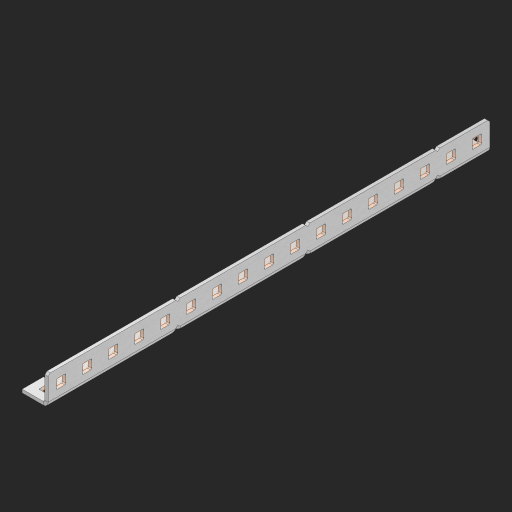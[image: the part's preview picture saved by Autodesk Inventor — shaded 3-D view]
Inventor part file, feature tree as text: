
AUTODESK INVENTOR PART (.ipt)
format: ipt  version: 2023 (Build 270158000, 158)  size: 903,168 bytes
history: native  units: in
note: dims shown in document units (in); Inventor stores cm internally (conversion verified against a paired STEP export)
features: other x199, extrude x49, sheet_metal_op x11, sketch x10, pattern_linear x2, mirror x1, chamfer x1
ambient origin geometry x8: Origin, YZ Plane, XZ Plane, XY Plane, X Axis, Y Axis, Z Axis, Center Point
bodies: Solid1 (feature_tree), Body (feature_tree)
feature tree (273):
  other  "Alu Half C 1x2x1x17"
  other  "Table"
  other  "Alu C 1x2x1x35"
  other  "Alu C 1x2x1x34"
  other  "Alu C 1x2x1x33"
  other  "Alu C 1x2x1x32"
  other  "Alu C 1x2x1x31"
  other  "Alu C 1x2x1x30"
  other  "Alu C 1x2x1x29"
  other  "Alu C 1x2x1x28"
  other  "Alu C 1x2x1x27"
  other  "Alu C 1x2x1x26"
  other  "Alu C 1x2x1x25"
  other  "Alu C 1x2x1x24"
  other  "Alu C 1x2x1x23"
  other  "Alu C 1x2x1x22"
  other  "Alu C 1x2x1x21"
  other  "Alu C 1x2x1x20"
  other  "Alu C 1x2x1x19"
  other  "Alu C 1x2x1x18"
  other  "Alu C 1x2x1x17"
  other  "Alu C 1x2x1x16"
  other  "Alu C 1x2x1x15"
  other  "Alu C 1x2x1x14"
  other  "Alu C 1x2x1x13"
  other  "Alu C 1x2x1x12"
  other  "Alu C 1x2x1x11"
  other  "Alu C 1x2x1x10"
  other  "Alu C 1x2x1x9"
  other  "Alu C 1x2x1x8"
  other  "Alu C 1x2x1x7"
  other  "Alu C 1x2x1x6"
  other  "Alu C 1x2x1x5"
  other  "Alu C 1x2x1x4"
  other  "Alu C 1x2x1x3"
  other  "Alu C 1x2x1x2"
  other  "Alu C 1x2x1x1"
  other  "Steel C 1x2x1x35"
  other  "Steel C 1x2x1x34"
  other  "Steel C 1x2x1x33"
  other  "Steel C 1x2x1x32"
  other  "Steel C 1x2x1x31"
  other  "Steel C 1x2x1x30"
  other  "Steel C 1x2x1x29"
  other  "Steel C 1x2x1x28"
  other  "Steel C 1x2x1x27"
  other  "Steel C 1x2x1x26"
  other  "Steel C 1x2x1x25"
  other  "Steel C 1x2x1x24"
  other  "Steel C 1x2x1x23"
  other  "Steel C 1x2x1x22"
  other  "Steel C 1x2x1x21"
  other  "Steel C 1x2x1x20"
  other  "Steel C 1x2x1x19"
  other  "Steel C 1x2x1x18"
  other  "Steel C 1x2x1x17"
  other  "Steel C 1x2x1x16"
  other  "Steel C 1x2x1x15"
  other  "Steel C 1x2x1x14"
  other  "Steel C 1x2x1x13"
  other  "Steel C 1x2x1x12"
  other  "Steel C 1x2x1x11"
  other  "Steel C 1x2x1x10"
  other  "Steel C 1x2x1x9"
  other  "Steel C 1x2x1x8"
  other  "Steel C 1x2x1x7"
  other  "Steel C 1x2x1x6"
  other  "Steel C 1x2x1x5"
  other  "Steel C 1x2x1x4"
  other  "Steel C 1x2x1x3"
  other  "Steel C 1x2x1x2"
  other  "Steel C 1x2x1x1"
  other  "Alu Half C 1x2x1x35"
  other  "Alu Half C 1x2x1x34"
  other  "Alu Half C 1x2x1x33"
  other  "Alu Half C 1x2x1x32"
  other  "Alu Half C 1x2x1x31"
  other  "Alu Half C 1x2x1x30"
  other  "Alu Half C 1x2x1x29"
  other  "Alu Half C 1x2x1x28"
  other  "Alu Half C 1x2x1x27"
  other  "Alu Half C 1x2x1x26"
  other  "Alu Half C 1x2x1x25"
  other  "Alu Half C 1x2x1x24"
  other  "Alu Half C 1x2x1x23"
  other  "Alu Half C 1x2x1x22"
  other  "Alu Half C 1x2x1x21"
  other  "Alu Half C 1x2x1x20"
  other  "Alu Half C 1x2x1x19"
  other  "Alu Half C 1x2x1x18"
  other  "Alu Half C 1x2x1x16"
  other  "Alu Half C 1x2x1x15"
  other  "Alu Half C 1x2x1x14"
  other  "Alu Half C 1x2x1x13"
  other  "Alu Half C 1x2x1x12"
  other  "Alu Half C 1x2x1x11"
  other  "Alu Half C 1x2x1x10"
  other  "Alu Half C 1x2x1x9"
  other  "Alu Half C 1x2x1x8"
  other  "Alu Half C 1x2x1x7"
  other  "Alu Half C 1x2x1x6"
  other  "Alu Half C 1x2x1x5"
  other  "Alu Half C 1x2x1x4"
  other  "Alu Half C 1x2x1x3"
  other  "Alu Half C 1x2x1x2"
  other  "Alu Half C 1x2x1x1"
  other  "Steel Half C 1x2x1x35"
  other  "Steel Half C 1x2x1x34"
  other  "Steel Half C 1x2x1x33"
  other  "Steel Half C 1x2x1x32"
  other  "Steel Half C 1x2x1x31"
  other  "Steel Half C 1x2x1x30"
  other  "Steel Half C 1x2x1x29"
  other  "Steel Half C 1x2x1x28"
  other  "Steel Half C 1x2x1x27"
  other  "Steel Half C 1x2x1x26"
  other  "Steel Half C 1x2x1x25"
  other  "Steel Half C 1x2x1x24"
  other  "Steel Half C 1x2x1x23"
  other  "Steel Half C 1x2x1x22"
  other  "Steel Half C 1x2x1x21"
  other  "Steel Half C 1x2x1x20"
  other  "Steel Half C 1x2x1x19"
  other  "Steel Half C 1x2x1x18"
  other  "Steel Half C 1x2x1x17"
  other  "Steel Half C 1x2x1x16"
  other  "Steel Half C 1x2x1x15"
  other  "Steel Half C 1x2x1x14"
  other  "Steel Half C 1x2x1x13"
  other  "Steel Half C 1x2x1x12"
  other  "Steel Half C 1x2x1x11"
  other  "Steel Half C 1x2x1x10"
  other  "Steel Half C 1x2x1x9"
  other  "Steel Half C 1x2x1x8"
  other  "Steel Half C 1x2x1x7"
  other  "Steel Half C 1x2x1x6"
  other  "Steel Half C 1x2x1x5"
  other  "Steel Half C 1x2x1x4"
  other  "Steel Half C 1x2x1x3"
  other  "Steel Half C 1x2x1x2"
  other  "Steel Half C 1x2x1x1"
  sheet_metal_op  "Flanges"
  other  "Flange Pattern Plane"
  other  "Flange Pattern Sketch"
  sheet_metal_op  "Flange Pattern"
  sheet_metal_op  "Body Pattern"
  pattern_linear  "Center Pattern"  Spacing1=0.0625in  [1 undecoded]
  other  "Arc Length"
  mirror  "Notch Mirror"
  pattern_linear  "Notch Pattern"  Spacing1=0.182in  [1 undecoded]
  chamfer  "End Chamfer"
  extrude  "Half Cut"  Depth=0.02in
  sketch  "Sketch1"  dims[d0=1.0in]
  other  "Plate1"
  sketch  "Sketch2"  dims[d1=8.5in]
  other  "Plate2"
  sheet_metal_op  "Bend1"
  sheet_metal_op  "Corner1"
  sketch  "Sketch3"  dims[d2=0.0625in]
  sketch  "Sketch7"  dims[d3=0.0625in]
  other  "Srf1"
  other  "Srf2"
  sketch  "Sketch8"  dims[d4=0.0312in]
  sketch  "Sketch9"  dims[d5=0.125in]
  other  "Srf91"
  sheet_metal_op  "Body Pattern Sketch"
  other  "Srf92"
  sketch  "Sketch13"  dims[d6=0.0625in]
  sketch  "Sketch14"  dims[d7=0.5in d8=90.0deg d9=0.0312in]
  sketch  "Sketch15"  dims[d10=0.25in]
  sketch  "Sketch16"  dims[d11=0.0625in d12=0.0625in d16=0.182in d17=0.02in d18=0.0625in d19=0.0in d20=0.25in d21=0.25in d38=6.6929in d40=0.5in d41=0.3937in d43=1.0in d46=0.172in d47=1.0in d48=0.0in d49=0.182in d50=0.02in d51=0.25in d52=0.25in d53=0.0625in d54=0.0in d55=0.172in d56=1.0in d57=0.0in d58=0.25in d60=6.6929in d62=0.5in d63=0.3937in d65=0.5in d85=0.1473in d86=0.1782in d88=0.04in d89=0.0625in d90=0.0in d91=0.04in d92=0.0491in d95=2.5in d96=0.04in d97=0.25in d98=45.0deg d99=0.25in d100=0.5in d101=0.0in d102=2.497in d106=0.182in d107=0.02in d108=0.5in d109=0.5in d110=0.0625in d111=0.0in d112=0.172in d113=0.5in d114=0.0in d117=0.5in d118=0.5in d119=0.5in]
  other  "Srf786"
  other  "Srf823"
  other  "Srf824"
  other  "Srf825"
  other  "Srf826"
  other  "Srf827"
  other  "Srf828"
  other  "Srf829"
  other  "Srf856"
  other  "Srf857"
  other  "Srf858"
  other  "Srf859"
  other  "Srf860"
  other  "Srf861"
  other  "Srf862"
  other  "Srf889"
  other  "Srf890"
  other  "Srf891"
  other  "Srf892"
  other  "Srf893"
  other  "Srf894"
  other  "Srf895"
  other  "Srf896"
  other  "Srf922"
  other  "Srf923"
  other  "Srf924"
  other  "Srf925"
  other  "Srf926"
  other  "Srf959"
  other  "Srf960"
  other  "Srf961"
  other  "Srf962"
  other  "Srf963"
  other  "Srf996"
  other  "Srf997"
  other  "Srf998"
  other  "Srf999"
  other  "Srf1000"
  other  "Srf1143"
  other  "Srf1144"
  other  "Srf1145"
  other  "Srf1199"
  other  "Srf1200"
  other  "Srf1201"
  other  "Srf1255"
  other  "Srf1256"
  other  "Srf1257"
  sheet_metal_op  "Flange Stamp"
  sheet_metal_op  "Flange Circle"
  sheet_metal_op  "Body Stamp"
  sheet_metal_op  "Body Circle"
  other  "Center Stamp"
  other  "Center Circle"
  sheet_metal_op  "Notch"
  extrude  "ExtrusionSrf2"  Depth=0.0625in
  extrude  "ExtrusionSrf92"  TaperAngle=0.0deg  [1 undecoded]
  extrude  "ExtrusionSrf823"  Depth=0.5in
  extrude  "ExtrusionSrf824"  Depth=0.5in
  extrude  "ExtrusionSrf825"  Depth=0.5in
  extrude  "ExtrusionSrf826"  Depth=0.5in
  extrude  "ExtrusionSrf827"  Depth=1.0in TaperAngle=0.0deg
  extrude  "ExtrusionSrf828"  Depth=0.182in
  extrude  "ExtrusionSrf829"  Depth=0.02in
  extrude  "ExtrusionSrf856"  Depth=0.5in
  extrude  "ExtrusionSrf857"  Depth=0.5in
  extrude  "ExtrusionSrf858"  Depth=0.0625in
  extrude  "ExtrusionSrf859"  TaperAngle=0.0deg  [1 undecoded]
  extrude  "ExtrusionSrf860"  Depth=0.5in
  extrude  "ExtrusionSrf861"  Depth=1.0in TaperAngle=0.0deg
  extrude  "ExtrusionSrf862"  Depth=0.5in
  extrude  "ExtrusionSrf889"  Depth=0.5in
  extrude  "ExtrusionSrf890"  Depth=0.5in
  extrude  "ExtrusionSrf891"  Depth=0.5in
  extrude  "ExtrusionSrf892"  Depth=0.5in
  extrude  "ExtrusionSrf893"  Depth=0.5in
  extrude  "ExtrusionSrf894"  Depth=0.0625in
  extrude  "ExtrusionSrf895"  TaperAngle=0.0deg  [1 undecoded]
  extrude  "ExtrusionSrf896"  Depth=0.5in
  extrude  "ExtrusionSrf922"  Depth=0.5in
  extrude  "ExtrusionSrf923"  Depth=0.5in
  extrude  "ExtrusionSrf924"  Depth=0.5in TaperAngle=45.0deg
  extrude  "ExtrusionSrf925"  Depth=0.5in
  extrude  "ExtrusionSrf926"  Depth=0.5in TaperAngle=0.0deg
  extrude  "ExtrusionSrf959"  Depth=0.5in
  extrude  "ExtrusionSrf960"  Depth=0.182in
  extrude  "ExtrusionSrf961"  Depth=0.02in
  extrude  "ExtrusionSrf962"  Depth=0.5in
  extrude  "ExtrusionSrf963"  Depth=0.5in
  extrude  "ExtrusionSrf996"  Depth=0.0625in
  extrude  "ExtrusionSrf997"  TaperAngle=0.0deg  [1 undecoded]
  extrude  "ExtrusionSrf998"  Depth=0.5in
  extrude  "ExtrusionSrf999"  Depth=0.5in TaperAngle=0.0deg
  extrude  "ExtrusionSrf1000"  Depth=0.5in
  extrude  "ExtrusionSrf1143"  Depth=0.5in
  extrude  "ExtrusionSrf1144"  Depth=0.5in
  extrude  "ExtrusionSrf1145"  [1 undecoded]
  extrude  "ExtrusionSrf1199"  [1 undecoded]
  extrude  "ExtrusionSrf1200"  [1 undecoded]
  extrude  "ExtrusionSrf1201"  [1 undecoded]
  extrude  "ExtrusionSrf1255"  [1 undecoded]
  extrude  "ExtrusionSrf1256"  [1 undecoded]
  extrude  "ExtrusionSrf1257"  [1 undecoded]
note: 13 required parameter values undecoded (feature->parameter linkage not recoverable at this tier; creation-order binding heuristic only, values carry confidence <= 0.55)
